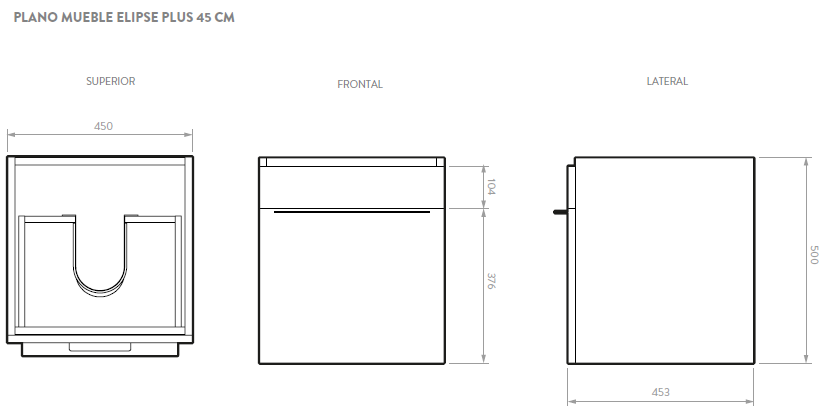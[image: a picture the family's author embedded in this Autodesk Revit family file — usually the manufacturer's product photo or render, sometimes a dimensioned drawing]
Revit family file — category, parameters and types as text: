
# Revit family: 135076841_Mueble Elipse Plus 60 cm con Lavamanos
name_source: partatom
category: Furniture
units: mm (PartAtom-declared; Revit-internal decimal feet)

## family parameters
Always vertical = Yes
Cut with Voids When Loaded = No
OmniClass Number = 23.31.13.11
OmniClass Title = Single Sinks
Room Calculation Point = No
Shared = No
Work Plane-Based = No

## types (1)
- 135076841_Mueble Elipse Plus 60 cm con Lavamanos
    Acabado = Corona_Ambar
    Alto = 500 mm  [stored 1.64042 ft]
    Ancho = 600 mm  [stored 1.9685 ft]
    Creado por = IDD
    Description = Línea de Muebles Elipse Plus con mezcla de materiales y manija en aluminio
que brindan un diseño moderno, en formato de 60 y 80 cm con una puerta y
una canastilla organizadora. Máxima capacidad de almacenamiento.
· Resistentes a la humedad.
· Lavamanos 100% en porcelana.
· Canastilla Organizadora
    Fecha de creación = 28/07/2020
    Garantía = 5 Años (Madera)
    Garantía Herraje = 1 año
    Longitud = 453 mm  [stored 1.48622 ft]
    Manija = Corona_Aluminio
    Manufacturer = Corona
    Material = Corona_Madera_Niebla
    Model = Elipse Plus 60
    Peso Bruto aprox = 43,9 lb (19,9 kg).
    Peso Neto aprox = 35,7 lb (16,2 kg).
    Resistencia a la humedad = 8%
    Resistencia al rayado = 700 ciclos
    URL = https://corona.co

note: [stored X ft] marks values corroborated as IEEE doubles in the binary element streams (Revit-internal decimal feet)

## geometry (parser evidence)
native form markers: Sweep x12
no freeform markers — native parametric forms only
